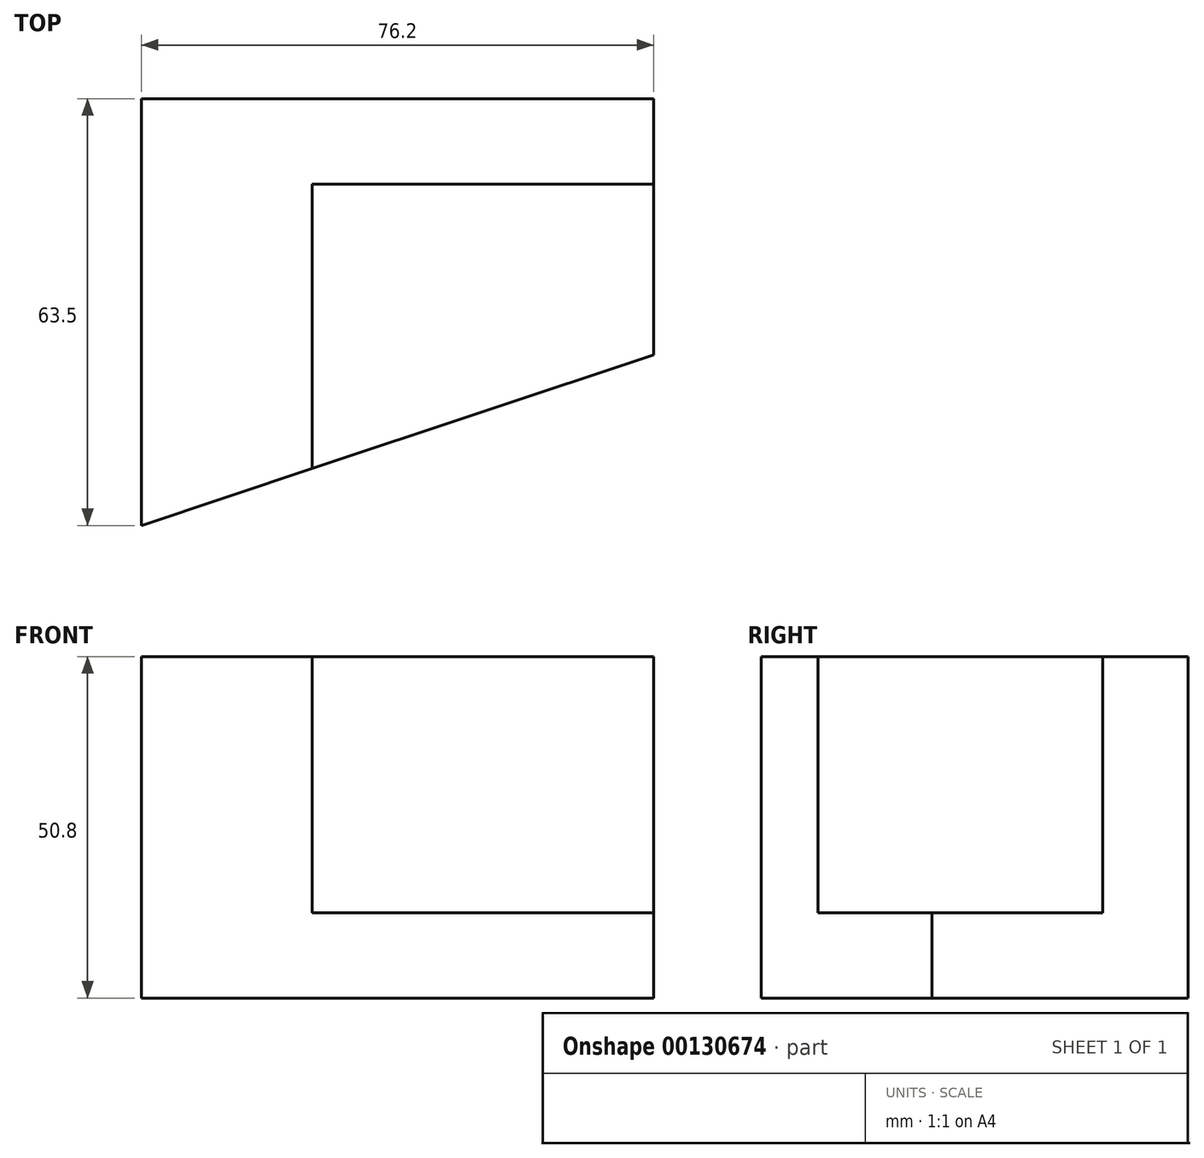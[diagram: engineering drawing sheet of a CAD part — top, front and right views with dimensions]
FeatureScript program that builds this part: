
annotation { "Feature Type Name" : "Feature", "Feature Type Description" : "" }
export const myFeature = defineFeature(function(context is Context, id is Id, definition is map)
    precondition{}
    {
        {
            var Q0;
            Q0=qCreatedBy(makeId("Front.planeOp"),FACE);
            var sketch = newSketch(context, id + "F0", { "sketchPlane" : qUnion([Q0])});
            skLineSegment(sketch, "E0.bottom", {"start": v(0, 0) * mm, "end": v(76.2, 0) * mm});
            skLineSegment(sketch, "E0.top", {"start": v(0, 50.8) * mm, "end": v(76.2, 50.8) * mm});
            skLineSegment(sketch, "E0.left", {"start": v(0, 0) * mm, "end": v(0, 50.8) * mm});
            skLineSegment(sketch, "E0.right", {"start": v(76.2, 0) * mm, "end": v(76.2, 50.8) * mm});
            skLineSegment(sketch, "E1.bottom", {"start": v(25.4, 50.8) * mm, "end": v(76.2, 50.8) * mm});
            skLineSegment(sketch, "E1.top", {"start": v(25.4, 12.7) * mm, "end": v(76.2, 12.7) * mm});
            skLineSegment(sketch, "E1.left", {"start": v(25.4, 50.8) * mm, "end": v(25.4, 12.7) * mm});
            skLineSegment(sketch, "E1.right", {"start": v(76.2, 50.8) * mm, "end": v(76.2, 12.7) * mm});
            skSolve(sketch);
        }
        {
            var Q0;
            Q0 = qSketchRegion(id + "F0", true);
            extrude(context, id + "F1", {"entities" : qUnion([Q0]), "depth" : 63.5 * mm});
        }
        {
            var Q0;
            Q0=makeQuery(id+"F1.opExtrude","CAP_FACE",FACE,{"disambiguationData":[OSD([sQuery(id+"F0.wireOp",EDGE,"E0.bottom"),sQuery(id+"F0.wireOp",EDGE,"E0.top"),sQuery(id+"F0.wireOp",EDGE,"E0.left"),sQuery(id+"F0.wireOp",EDGE,"E0.right"),sQuery(id+"F0.wireOp",EDGE,"E1.bottom"),sQuery(id+"F0.wireOp",EDGE,"E1.right")])],"isStart":false});
            var sketch = newSketch(context, id + "F2", { "sketchPlane" : qUnion([Q0])});
            skLineSegment(sketch, "E2.0", {"start": v(25.4, 50.8) * mm, "end": v(25.4, 12.7) * mm});
            skLineSegment(sketch, "E3.0", {"start": v(25.4, 12.7) * mm, "end": v(76.2, 12.7) * mm});
            skLineSegment(sketch, "E4.0", {"start": v(76.2, 50.8) * mm, "end": v(76.2, 12.7) * mm});
            skLineSegment(sketch, "E5.0", {"start": v(25.4, 50.8) * mm, "end": v(76.2, 50.8) * mm});
            skSolve(sketch);
        }
        {
            var Q0;
            Q0 = qSketchRegion(id + "F2", true);
            extrude(context, id + "F3", {"entities" : qUnion([Q0]), "operationType" : NewBodyOperationType.REMOVE, "oppositeDirection" : true, "depth" : 50.8 * mm});
        }
        {
            var Q0;
            Q0=makeQuery(id+"F1.opExtrude","SWEPT_FACE",FACE,{"disambiguationData":[OSD([sQuery(id+"F0.wireOp",EDGE,"E0.top"),sQuery(id+"F0.wireOp",EDGE,"E1.bottom")])]});
            var sketch = newSketch(context, id + "F4", { "sketchPlane" : qUnion([Q0])});
            skLineSegment(sketch, "E6", {"start": v(0, -63.5) * mm, "end": v(76.2, -38.1) * mm});
            skLineSegment(sketch, "E7", {"start": v(76.2, -38.1) * mm, "end": v(76.2, -63.5) * mm});
            skLineSegment(sketch, "E8", {"start": v(76.2, -63.5) * mm, "end": v(0, -63.5) * mm});
            skSolve(sketch);
        }
        {
            var Q0;
            Q0 = qSketchRegion(id + "F4", true);
            extrude(context, id + "F5", {"entities" : qUnion([Q0]), "operationType" : NewBodyOperationType.REMOVE, "endBound" : BoundingType.THROUGH_ALL, "oppositeDirection" : true, "depth" : 25.4 * mm});
        }
    });
